# Revit family: Wenger Cabinet 42
name_source: partatom
category: Furniture
revit_build: Autodesk Revit Architecture 2012 (Build: 20110916_2132(x64)
units: mm (PartAtom-declared; Revit-internal decimal feet)

## types (14) — shared parameters
Cabinet Height = 7' - 1 5/8"
Cabinet Width = 5' - 0 1/4"
Manufacturer = Wenger Corporation
URL = http://www.wengercorp.com

## per-type parameters (varying)
| type | Cabinet Back Thickness | Cabinet Depth | Cabinet Label | Description | Model | Pack Style |
| Standard Cabinet #42 - Bass | 0' - 0 3/4" | 3' - 3 1/4" | Labels : Standard | Standard Cabinet #42 - Basses | 42 - Bass | Bass |
| Acoustic Cabinet #42 - Bass | 0' - 3 1/4" | 3' - 5 3/4" | Labels : Acoustic | Acoustic Cabinet #42 - Basses | 42A - Bass | Bass |
| Standard Cabinet #42 - Cello | 0' - 0 3/4" | 3' - 3 1/4" | Labels : Standard | Standard Cabinet #42 - Cellos | 42 - Cello | Cello |
| Standard Cabinet #42 - Guitarron | 0' - 0 3/4" | 3' - 3 1/4" | Labels : Standard | Standard Cabinet #42 - Guitarrons | 42 - Guitarron | Guitarron |
| Standard Cabinet #42 - Guitar | 0' - 0 3/4" | 3' - 3 1/4" | Labels : Standard | Standard Cabinet #42 - Guitars | 42 - Guitar | Guitar |
| Standard Cabinet #42 - Violins/Violas/Vihuelas | 0' - 0 3/4" | 3' - 3 1/4" | Labels : Standard | Standard Cabinet #42 - Violins/Violas/Vihuelas | 42 - Violins/Violas/Vihuelas | Violins-Violas-Vihuelas |
| Standard Cabinet #42 - VVV Hi Pack | 0' - 0 3/4" | 3' - 3 1/4" | Labels : Standard | Standard Cabinet #42 - VVV Hi Pack | 42 - VVV Hi Pack | VVV High Pack |
| Standard Cabinet #42 - Combo | 0' - 0 3/4" | 3' - 3 1/4" | Labels : Standard | Standard Cabinet #42 - Combo | 42 - Combo | Combo |
| Acoustic Cabinet #42 - Cello | 0' - 3 1/4" | 3' - 5 3/4" | Labels : Acoustic | Acoustic Cabinet #42 - Cellos | 42A - Cello | Cello |
| Acoustic Cabinet #42 - Combo | 0' - 3 1/4" | 3' - 5 3/4" | Labels : Acoustic | Acoustic Cabinet #42 - Combo | 42A - Combo | Combo |
| Acoustic Cabinet #42 - Guitar | 0' - 3 1/4" | 3' - 5 3/4" | Labels : Acoustic | Acoustic Cabinet #42 - Guitar | 42A - Guitar | Guitar |
| Acoustic Cabinet #42 - Guitarron | 0' - 3 1/4" | 3' - 5 3/4" | Labels : Acoustic | Acoustic Cabinet #42 - Guitarron | 42A - Guitarron | Guitarron |
| Acoustic Cabinet #42 - Violins/Violas/Vihuelas | 0' - 3 1/4" | 3' - 5 3/4" | Labels : Acoustic | Acoustic Cabinet #42 - Violins/Violas/Vihuelas | 42A - Violins/Violas/Vihuelas | Violins-Violas-Vihuelas |
| Acoustic Cabinet #42 - VVV Hi Pack | 0' - 3 1/4" | 3' - 5 3/4" | Labels : Acoustic | Acoustic Cabinet #42 - VVV Hi Pack | 42A - VVV Hi Pack | VVV High Pack |

## geometry (parser evidence)
native form markers: Blend x12, Sweep x21
no freeform markers — native parametric forms only
